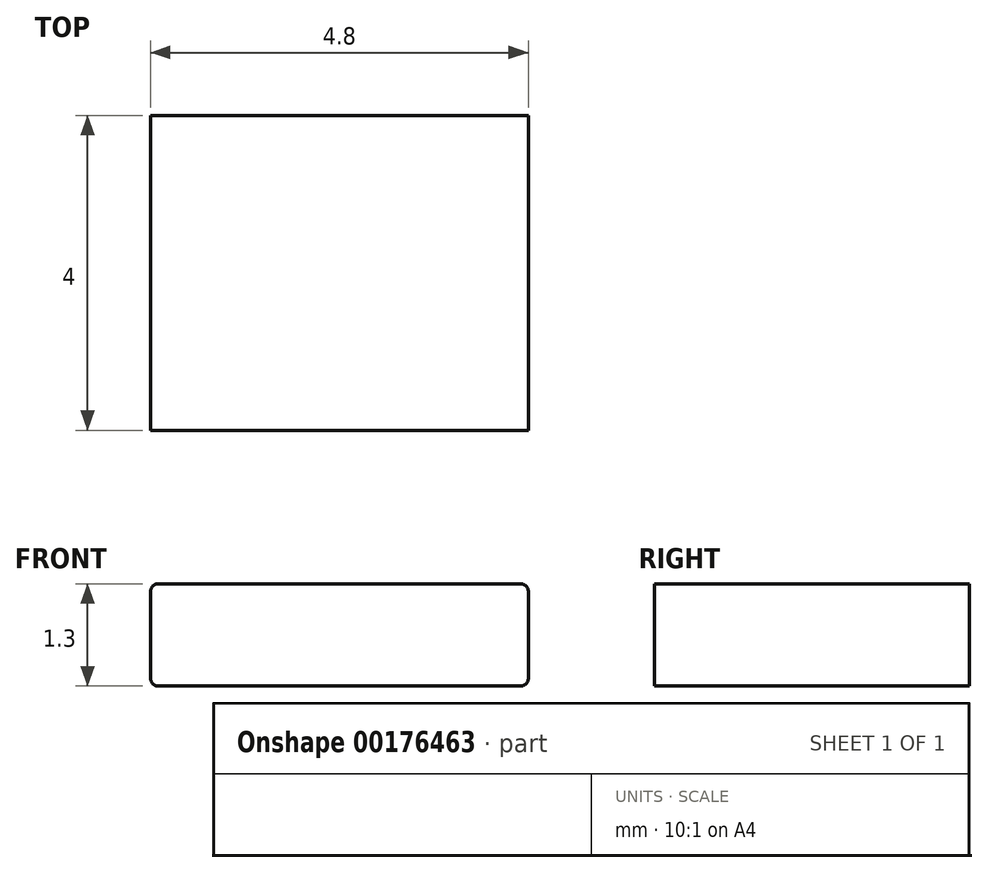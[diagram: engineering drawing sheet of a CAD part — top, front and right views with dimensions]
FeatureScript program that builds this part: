
annotation { "Feature Type Name" : "Feature", "Feature Type Description" : "" }
export const myFeature = defineFeature(function(context is Context, id is Id, definition is map)
    precondition{}
    {
        {
            var Q0;
            Q0=qCreatedBy(makeId("Front.planeOp"),FACE);
            var sketch = newSketch(context, id + "F0", { "sketchPlane" : qUnion([Q0])});
            skLineSegment(sketch, "E0.bottom", {"start": v(-2.4, 0.65) * mm, "end": v(2.4, 0.65) * mm});
            skLineSegment(sketch, "E0.top", {"start": v(-2.4, -0.65) * mm, "end": v(2.4, -0.65) * mm});
            skLineSegment(sketch, "E0.left", {"start": v(-2.4, 0.65) * mm, "end": v(-2.4, -0.65) * mm});
            skLineSegment(sketch, "E0.right", {"start": v(2.4, 0.65) * mm, "end": v(2.4, -0.65) * mm});
            skPoint(sketch, "E0.middle", {"position": v(0, 0) * mm});
            skSolve(sketch);
        }
        {
            var Q0;
            Q0=makeQuery(id+"F0.imprint","IMPRINT",FACE,{"disambiguationData":[TD([[makeQuery(id+"F0.imprint","IMPRINT",EDGE,{"derivedFrom":sQuery(id+"F0.wireOp",EDGE,"E0.bottom")}),-1.0]])]});
            extrude(context, id + "F1", {"entities" : qUnion([Q0]), "depth" : 4 * mm});
        }
        {
            var Q0;
            Q0=makeQuery(id+"F1.opExtrude","SWEPT_EDGE",EDGE,{"disambiguationData":[OSD([sQuery(id+"F0.wireOp",EDGE,"E0.bottom"),sQuery(id+"F0.wireOp",EDGE,"E0.right")])]});
            var Q1;
            Q1=makeQuery(id+"F1.opExtrude","SWEPT_EDGE",EDGE,{"disambiguationData":[OSD([sQuery(id+"F0.wireOp",EDGE,"E0.bottom"),sQuery(id+"F0.wireOp",EDGE,"E0.left")])]});
            var Q2;
            Q2=makeQuery(id+"F1.opExtrude","SWEPT_EDGE",EDGE,{"disambiguationData":[OSD([sQuery(id+"F0.wireOp",EDGE,"E0.top"),sQuery(id+"F0.wireOp",EDGE,"E0.left")])]});
            var Q3;
            Q3=makeQuery(id+"F1.opExtrude","SWEPT_EDGE",EDGE,{"disambiguationData":[OSD([sQuery(id+"F0.wireOp",EDGE,"E0.top"),sQuery(id+"F0.wireOp",EDGE,"E0.right")])]});
            fillet(context, id + "F2", {"entities" : qUnion([Q0, Q1, Q2, Q3]), "radius" : 0.1 * mm, "tangentPropagation" : true, "allowEdgeOverflow" : false});
        }
    });
